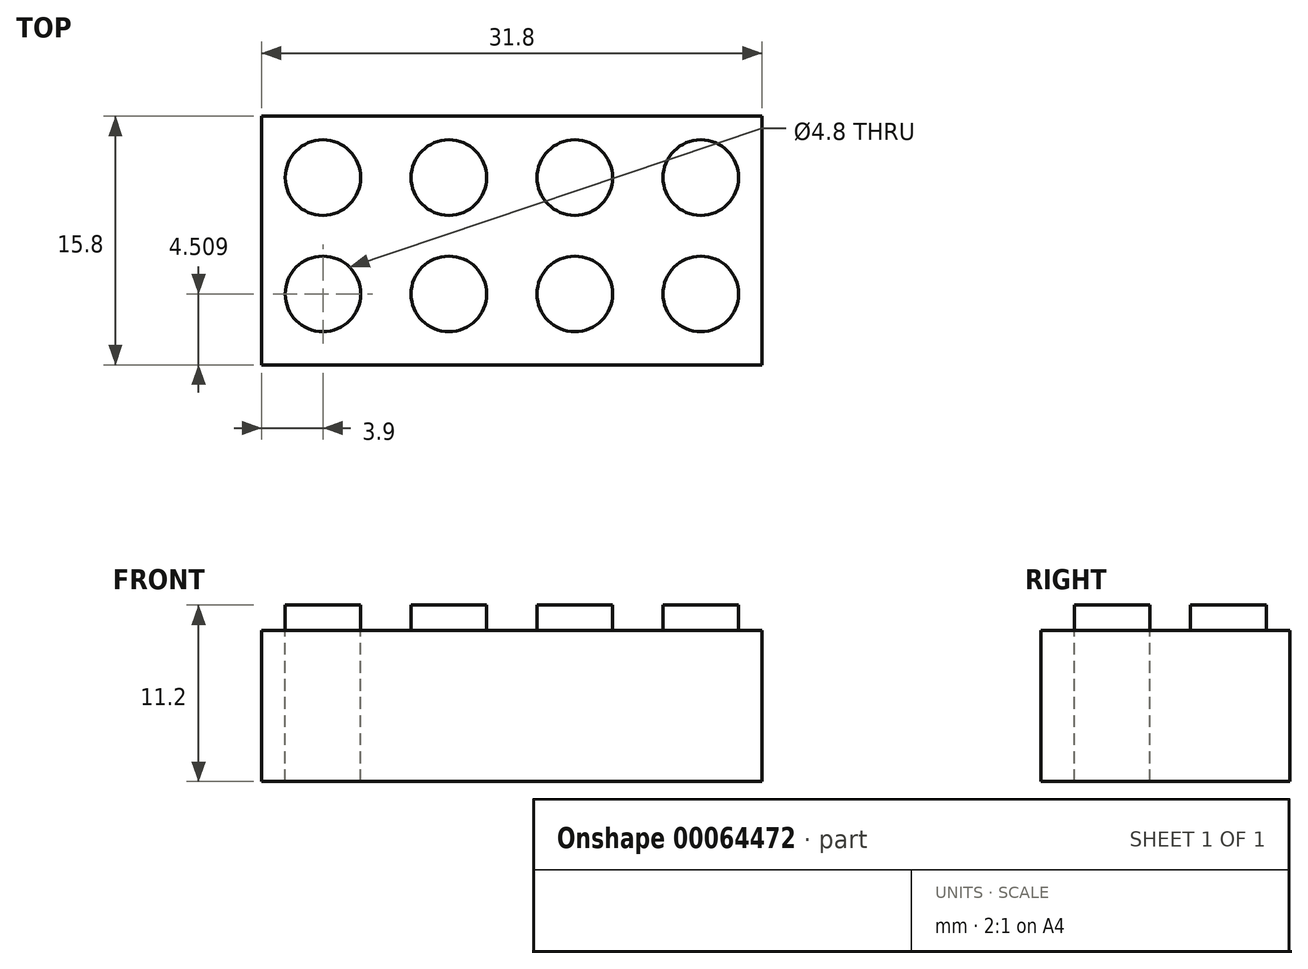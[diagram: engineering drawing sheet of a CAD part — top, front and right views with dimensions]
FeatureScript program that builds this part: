
annotation { "Feature Type Name" : "Feature", "Feature Type Description" : "" }
export const myFeature = defineFeature(function(context is Context, id is Id, definition is map)
    precondition{}
    {
        {
            var Q0;
            Q0=qCreatedBy(makeId("Top.planeOp"),FACE);
            var sketch = newSketch(context, id + "F0", { "sketchPlane" : qUnion([Q0])});
            skLineSegment(sketch, "E0.rect.bottom", {"start": v(15.9, -7.9) * mm, "end": v(-15.9, -7.9) * mm});
            skLineSegment(sketch, "E0.rect.top", {"start": v(15.9, 7.9) * mm, "end": v(-15.9, 7.9) * mm});
            skLineSegment(sketch, "E0.rect.left", {"start": v(15.9, -7.9) * mm, "end": v(15.9, 7.9) * mm});
            skLineSegment(sketch, "E0.rect.right", {"start": v(-15.9, -7.9) * mm, "end": v(-15.9, 7.9) * mm});
            skPoint(sketch, "E0.rect.middle", {"position": v(0, 0) * mm});
            skCircle(sketch, "E1", {"center": v(-12, 4) * mm, "radius": 2.4 * mm});
            skCircle(sketch, "E2.0.1.0", {"center": v(-12, -3.4) * mm, "radius": 2.4 * mm});
            skCircle(sketch, "E2.1.0.0", {"center": v(-4, 4) * mm, "radius": 2.4 * mm});
            skCircle(sketch, "E2.1.1.0", {"center": v(-4, -3.4) * mm, "radius": 2.4 * mm});
            skCircle(sketch, "E2.2.0.0", {"center": v(4, 4) * mm, "radius": 2.4 * mm});
            skCircle(sketch, "E2.2.1.0", {"center": v(4, -3.4) * mm, "radius": 2.4 * mm});
            skCircle(sketch, "E2.3.0.0", {"center": v(12, 4) * mm, "radius": 2.4 * mm});
            skCircle(sketch, "E2.3.1.0", {"center": v(12, -3.4) * mm, "radius": 2.4 * mm});
            skLineSegment(sketch, "E2.direction1", {"start": v(-12, 4) * mm, "end": v(-4, 4) * mm, "construction": true});
            skLineSegment(sketch, "E2.direction2", {"start": v(-12, 4) * mm, "end": v(-12, -3.4) * mm, "construction": true});
            skSolve(sketch);
        }
        {
            var Q0;
            Q0=makeQuery(id+"F0.imprint","IMPRINT",FACE,{"disambiguationData":[TD([[makeQuery(id+"F0.imprint","IMPRINT",EDGE,{"derivedFrom":sQuery(id+"F0.wireOp",EDGE,"E2.0.1.0")}),1.0]])]});
            var Q1;
            Q1=makeQuery(id+"F0.imprint","IMPRINT",FACE,{"disambiguationData":[TD([[makeQuery(id+"F0.imprint","IMPRINT",EDGE,{"derivedFrom":sQuery(id+"F0.wireOp",EDGE,"E1")}),1.0]])]});
            var Q2;
            Q2=makeQuery(id+"F0.imprint","IMPRINT",FACE,{"disambiguationData":[TD([[makeQuery(id+"F0.imprint","IMPRINT",EDGE,{"derivedFrom":sQuery(id+"F0.wireOp",EDGE,"E2.1.0.0")}),1.0]])]});
            var Q3;
            Q3=makeQuery(id+"F0.imprint","IMPRINT",FACE,{"disambiguationData":[TD([[makeQuery(id+"F0.imprint","IMPRINT",EDGE,{"derivedFrom":sQuery(id+"F0.wireOp",EDGE,"E2.1.1.0")}),1.0]])]});
            var Q4;
            Q4=makeQuery(id+"F0.imprint","IMPRINT",FACE,{"disambiguationData":[TD([[makeQuery(id+"F0.imprint","IMPRINT",EDGE,{"derivedFrom":sQuery(id+"F0.wireOp",EDGE,"E2.2.1.0")}),1.0]])]});
            var Q5;
            Q5=makeQuery(id+"F0.imprint","IMPRINT",FACE,{"disambiguationData":[TD([[makeQuery(id+"F0.imprint","IMPRINT",EDGE,{"derivedFrom":sQuery(id+"F0.wireOp",EDGE,"E2.2.0.0")}),1.0]])]});
            var Q6;
            Q6=makeQuery(id+"F0.imprint","IMPRINT",FACE,{"disambiguationData":[TD([[makeQuery(id+"F0.imprint","IMPRINT",EDGE,{"derivedFrom":sQuery(id+"F0.wireOp",EDGE,"E2.3.0.0")}),1.0]])]});
            var Q7;
            Q7=makeQuery(id+"F0.imprint","IMPRINT",FACE,{"disambiguationData":[TD([[makeQuery(id+"F0.imprint","IMPRINT",EDGE,{"derivedFrom":sQuery(id+"F0.wireOp",EDGE,"E2.3.1.0")}),1.0]])]});
            extrude(context, id + "F1", {"entities" : qUnion([Q0, Q1, Q2, Q3, Q4, Q5, Q6, Q7]), "depth" : 1.6 * mm});
        }
        {
            var Q0;
            Q0=makeQuery(id+"F1.opExtrude","CAP_FACE",FACE,{"disambiguationData":[OSD([sQuery(id+"F0.wireOp",EDGE,"E2.0.1.0")])],"isStart":true});
            var sketch = newSketch(context, id + "F2", { "sketchPlane" : qUnion([Q0])});
            skLineSegment(sketch, "E3.rect.bottom", {"start": v(-15.9, -7.9) * mm, "end": v(15.9, -7.9) * mm});
            skLineSegment(sketch, "E3.rect.top", {"start": v(-15.9, 7.9) * mm, "end": v(15.9, 7.9) * mm});
            skLineSegment(sketch, "E3.rect.left", {"start": v(-15.9, -7.9) * mm, "end": v(-15.9, 7.9) * mm});
            skLineSegment(sketch, "E3.rect.right", {"start": v(15.9, -7.9) * mm, "end": v(15.9, 7.9) * mm});
            skPoint(sketch, "E3.rect.middle", {"position": v(0, 0) * mm});
            skLineSegment(sketch, "E4.rect.bottom", {"start": v(-14.8, 6.87) * mm, "end": v(14.8, 6.87) * mm});
            skLineSegment(sketch, "E4.rect.top", {"start": v(-14.8, -6.87) * mm, "end": v(14.8, -6.87) * mm});
            skLineSegment(sketch, "E4.rect.left", {"start": v(-14.8, 6.87) * mm, "end": v(-14.8, -6.87) * mm});
            skLineSegment(sketch, "E4.rect.right", {"start": v(14.8, 6.87) * mm, "end": v(14.8, -6.87) * mm});
            skSolve(sketch);
        }
        {
            var Q0;
            Q0=makeQuery(id+"F2.imprint","IMPRINT",FACE,{"disambiguationData":[TD([[makeQuery(id+"F2.imprint","IMPRINT",EDGE,{"derivedFrom":sQuery(id+"F2.wireOp",EDGE,"E3.rect.bottom")}),1.0]])]});
            var Q1;
            Q1=makeQuery(id+"F2.imprint","IMPRINT",FACE,{"disambiguationData":[TD([[makeQuery(id+"F2.imprint","IMPRINT",EDGE,{"derivedFrom":sQuery(id+"F2.wireOp",EDGE,"E4.rect.bottom")}),-1.0]])]});
            extrude(context, id + "F3", {"entities" : qUnion([Q0, Q1]), "operationType" : NewBodyOperationType.ADD, "depth" : 9.6 * mm});
        }
    });
